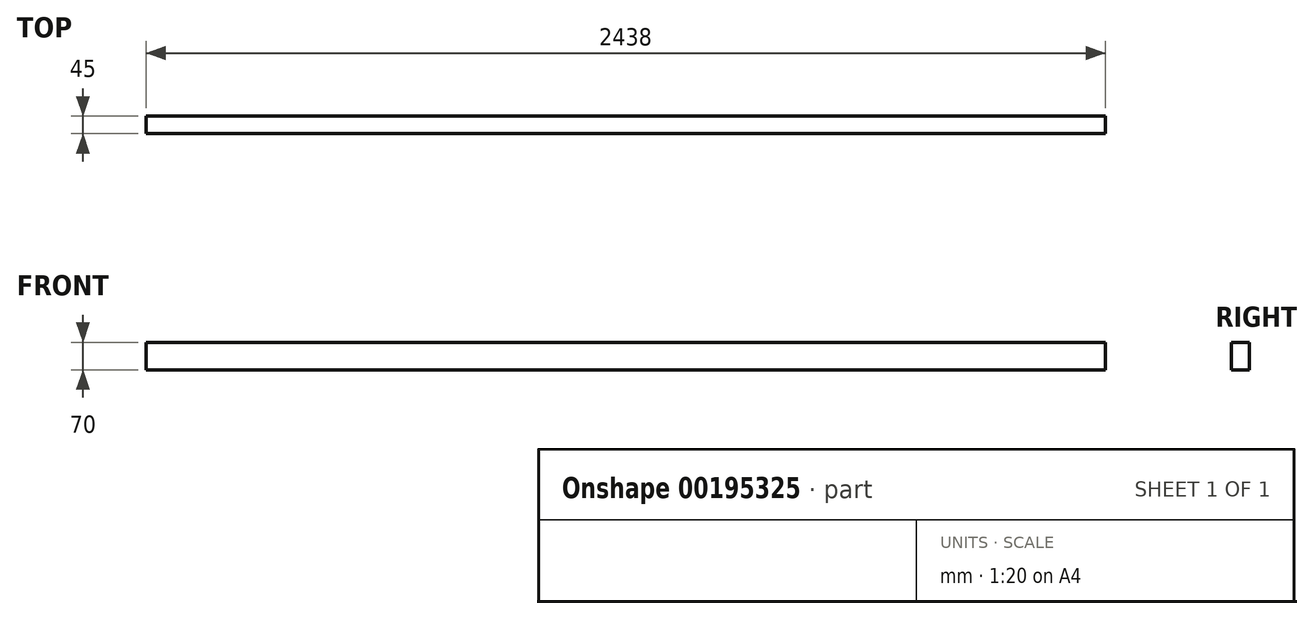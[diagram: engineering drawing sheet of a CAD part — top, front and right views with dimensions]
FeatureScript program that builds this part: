
annotation { "Feature Type Name" : "Feature", "Feature Type Description" : "" }
export const myFeature = defineFeature(function(context is Context, id is Id, definition is map)
    precondition{}
    {
        {
            var Q0;
            Q0=qCreatedBy(makeId("Top.planeOp"),FACE);
            var sketch = newSketch(context, id + "F0", { "sketchPlane" : qUnion([Q0])});
            skLineSegment(sketch, "E0.bottom", {"start": v(0, 0) * mm, "end": v(2438, 0) * mm});
            skLineSegment(sketch, "E0.top", {"start": v(0, -45) * mm, "end": v(2438, -45) * mm});
            skLineSegment(sketch, "E0.left", {"start": v(0, 0) * mm, "end": v(0, -45) * mm});
            skLineSegment(sketch, "E0.right", {"start": v(2438, 0) * mm, "end": v(2438, -45) * mm});
            skSolve(sketch);
        }
        {
            var Q0;
            Q0=makeQuery(id+"F0.imprint","IMPRINT",FACE,{"disambiguationData":[TD([[makeQuery(id+"F0.imprint","IMPRINT",EDGE,{"derivedFrom":sQuery(id+"F0.wireOp",EDGE,"E0.bottom")}),-1.0]])]});
            extrude(context, id + "F1", {"entities" : qUnion([Q0]), "depth" : 70 * mm});
        }
    });
